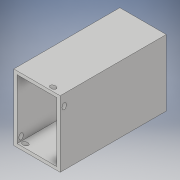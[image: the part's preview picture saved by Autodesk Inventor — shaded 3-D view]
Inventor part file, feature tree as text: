
AUTODESK INVENTOR PART (.ipt)
format: ipt  version: 2019 (Build 230136000, 136)  size: 165,376 bytes
history: native  units: mm
features: extrude x7, sketch x6
ambient origin geometry x8: Origin, YZ Plane, XZ Plane, XY Plane, X Axis, Y Axis, Z Axis, Center Point
bodies: Volumenkörper1 (feature_tree)
feature tree (13):
  sketch  "Skizze1"  dims[d0=45.0mm d1=30.0mm]
  extrude  "Extrusion1"  Depth=30.0mm
  extrude  "Extrusion2"  Depth=2.5mm TaperAngle=0.0deg
  extrude  "Extrusion3"  Depth=77.5mm
  extrude  "Extrusion4"  Depth=77.5mm
  extrude  "Extrusion5"  Depth=3.3mm
  extrude  "Extrusion6"  Depth=4.0mm
  extrude  "Extrusion7"  Depth=4.0mm
  sketch  "Skizze2"  dims[d2=2.5mm d3=2.5mm d4=0.0mm]
  sketch  "Skizze3"  dims[d5=77.5mm d6=0.0mm d7=3.0mm]
  sketch  "Skizze4"  dims[d8=77.5mm d9=0.0mm d11=6.0mm]
  sketch  "Skizze5"  dims[d12=6.0mm d13=0.0mm d14=3.3mm]
  sketch  "Skizze6"  dims[d15=6.0mm d16=0.0mm d17=4.0mm d18=4.0mm d19=3.3mm d20=6.0mm d21=0.0mm d22=6.0mm d23=0.0mm]
